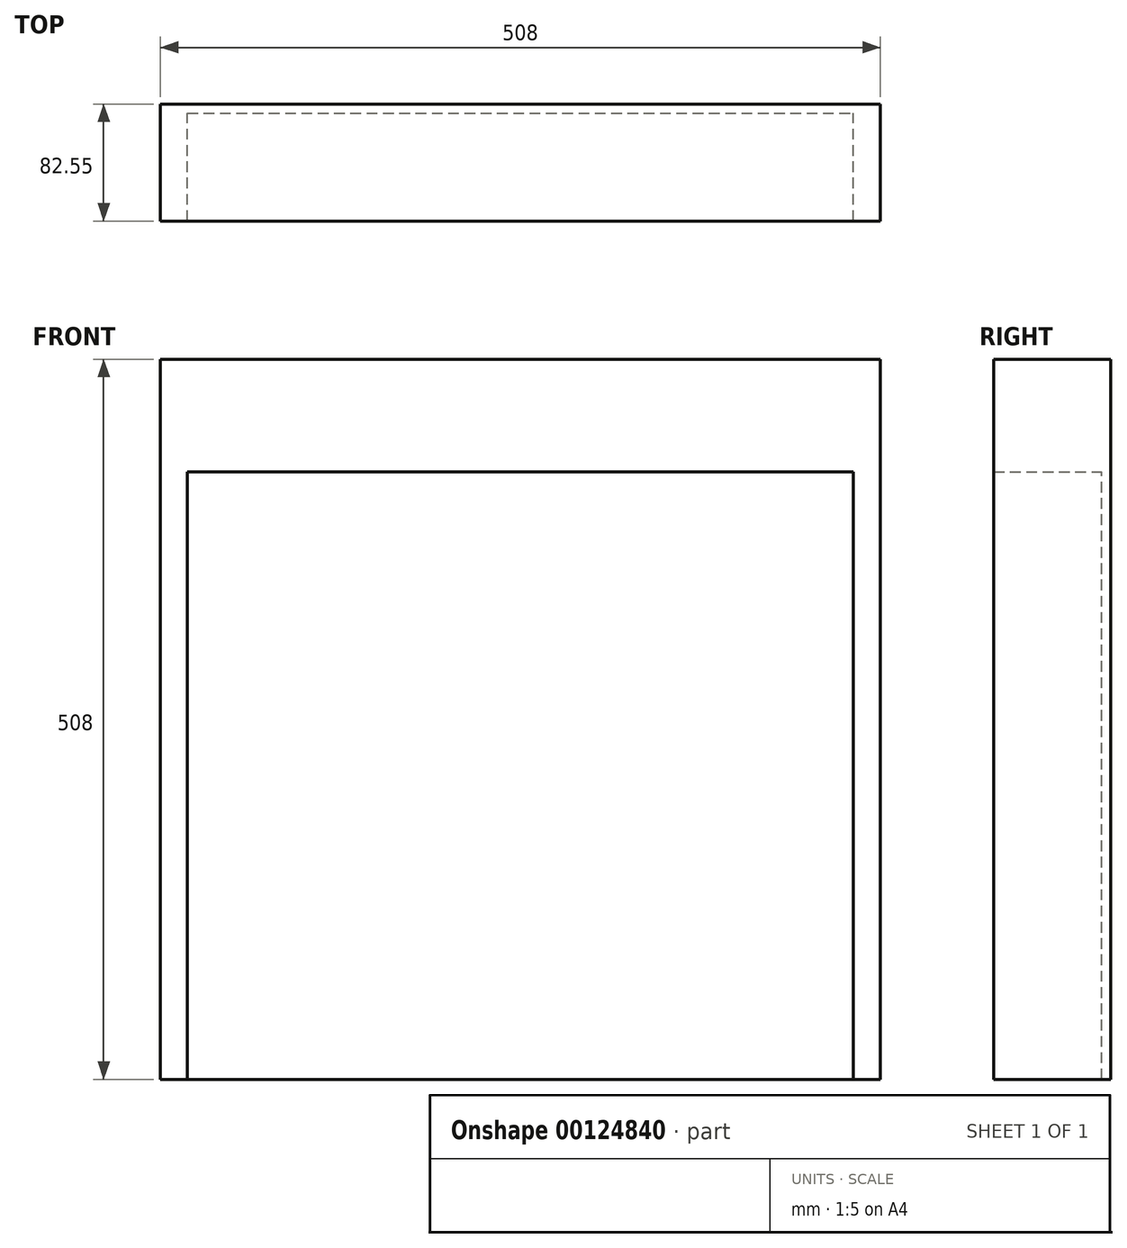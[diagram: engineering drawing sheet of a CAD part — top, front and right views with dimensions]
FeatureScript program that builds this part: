
annotation { "Feature Type Name" : "Feature", "Feature Type Description" : "" }
export const myFeature = defineFeature(function(context is Context, id is Id, definition is map)
    precondition{}
    {
        {
            var Q0;
            Q0=qCreatedBy(makeId("Front.planeOp"),FACE);
            var sketch = newSketch(context, id + "F0", { "sketchPlane" : qUnion([Q0])});
            skLineSegment(sketch, "E0.bottom", {"start": v(0, 508) * mm, "end": v(508, 508) * mm});
            skLineSegment(sketch, "E0.top", {"start": v(0, 0) * mm, "end": v(508, 0) * mm});
            skLineSegment(sketch, "E0.left", {"start": v(0, 508) * mm, "end": v(0, 0) * mm});
            skLineSegment(sketch, "E0.right", {"start": v(508, 508) * mm, "end": v(508, 0) * mm});
            skSolve(sketch);
        }
        {
            assignVariable(context, id + "F1", {"name" : "big_d", "anyValue" : 3.12});
        }
        {
            var Q0;
            Q0=makeQuery(id+"F0.imprint","IMPRINT",FACE,{"disambiguationData":[TD([[makeQuery(id+"F0.imprint","IMPRINT",EDGE,{"derivedFrom":sQuery(id+"F0.wireOp",EDGE,"E0.bottom")}),-1.0]])]});
            extrude(context, id + "F2", {"entities" : qUnion([Q0]), "depth" : 6.35 * mm});
        }
        {
            var Q0;
            Q0=makeQuery(id+"F2.opExtrude","CAP_FACE",FACE,{"disambiguationData":[OSD([sQuery(id+"F0.wireOp",EDGE,"E0.bottom"),sQuery(id+"F0.wireOp",EDGE,"E0.top"),sQuery(id+"F0.wireOp",EDGE,"E0.left"),sQuery(id+"F0.wireOp",EDGE,"E0.right")])],"isStart":false});
            var sketch = newSketch(context, id + "F3", { "sketchPlane" : qUnion([Q0])});
            skLineSegment(sketch, "E1.bottom", {"start": v(0, 0) * mm, "end": v(19.05, 0) * mm});
            skLineSegment(sketch, "E1.top", {"start": v(0, 508) * mm, "end": v(19.05, 508) * mm});
            skLineSegment(sketch, "E1.left", {"start": v(0, 0) * mm, "end": v(0, 508) * mm});
            skLineSegment(sketch, "E1.right", {"start": v(19.05, 0) * mm, "end": v(19.05, 508) * mm});
            skLineSegment(sketch, "E2.bottom", {"start": v(508, 508) * mm, "end": v(488.95, 508) * mm});
            skLineSegment(sketch, "E2.top", {"start": v(508, 0) * mm, "end": v(488.95, 0) * mm});
            skLineSegment(sketch, "E2.left", {"start": v(508, 508) * mm, "end": v(508, 0) * mm});
            skLineSegment(sketch, "E2.right", {"start": v(488.95, 508) * mm, "end": v(488.95, 0) * mm});
            skLineSegment(sketch, "E3.bottom", {"start": v(19.05, 508) * mm, "end": v(488.95, 508) * mm});
            skLineSegment(sketch, "E3.top", {"start": v(19.05, 428.63) * mm, "end": v(488.95, 428.63) * mm});
            skLineSegment(sketch, "E3.left", {"start": v(19.05, 508) * mm, "end": v(19.05, 428.63) * mm});
            skLineSegment(sketch, "E3.right", {"start": v(488.95, 508) * mm, "end": v(488.95, 428.63) * mm});
            skSolve(sketch);
        }
        {
            var Q0;
            Q0 = qSketchRegion(id + "F3", true);
            extrude(context, id + "F4", {"entities" : qUnion([Q0]), "operationType" : NewBodyOperationType.ADD, "depth" : 76.2 * mm});
        }
    });
